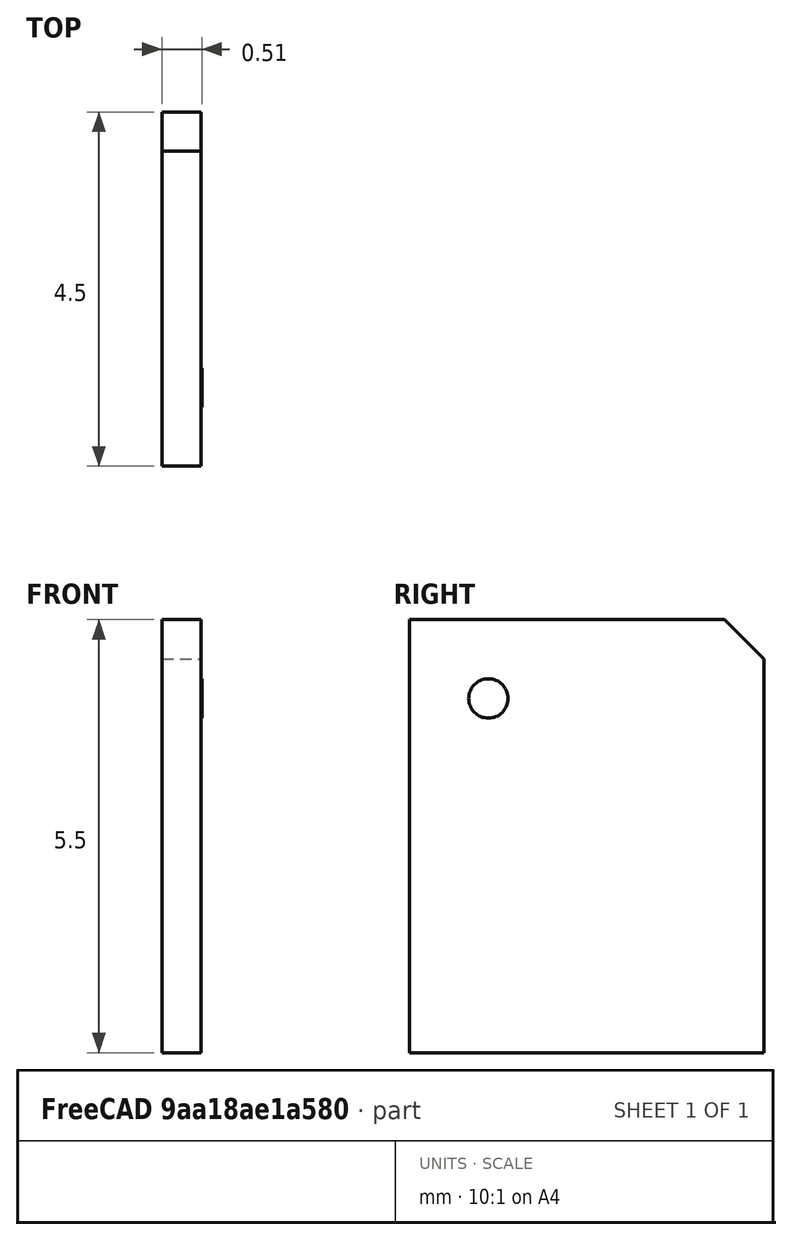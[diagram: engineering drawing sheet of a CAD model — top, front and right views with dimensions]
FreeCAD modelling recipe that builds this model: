
FCSTD DOCUMENT  (FreeCAD 1.1R20260108 (Git shallow))
Label: LiNbO3_Substrate_5mm
License: All rights reserved
LicenseURL: https://en.wikipedia.org/wiki/All_rights_reserved
objects: TechDraw::DrawViewAnnotation×5, TechDraw::DrawViewDimension×4, Sketcher::SketchObject×2, PartDesign::Pad×2, TechDraw::DrawProjGroupItem×2, App::Point×1, TechDraw::DrawSVGTemplate×1, PartDesign::Body×1, TechDraw::DrawProjGroup×1, TechDraw::DrawPage×1
note: 19 computed .brp shape members not serialized (recipe doc carries the construction recipe); baked Part::Feature solids carry a one-line shape summary decoded from their .brp

FEATURE [App::Point] Origin001
  Role = Origin
FEATURE [Sketcher::SketchObject] Sketch
  ArcFitTolerance = 1e-06
  AttachmentSupport = -> [Origin]
  ExternalTypes = [0]
  FullyConstrained = true
  MakeInternals = false
  MapMode = 5
  Placement = pos=(0,0,0) rot=(0.57735,0.57735,0.57735;2.0944rad)
  sketch-geometry (9):
    g0: LineSegment [constr] StartX=-2.25 StartY=-2.75 StartZ=0 EndX=2.25 EndY=-2.75 EndZ=0
    g1: LineSegment [constr] StartX=2.25 StartY=-2.75 StartZ=0 EndX=2.25 EndY=2.75 EndZ=0
    g2: LineSegment [constr] StartX=2.25 StartY=2.75 StartZ=0 EndX=-2.25 EndY=2.75 EndZ=0
    g3: LineSegment [constr] StartX=-2.25 StartY=2.75 StartZ=0 EndX=-2.25 EndY=-2.75 EndZ=0
    g4: LineSegment StartX=-2.25 StartY=-2.75 StartZ=0 EndX=2.25 EndY=-2.75 EndZ=0
    g5: LineSegment StartX=2.25 StartY=-2.75 StartZ=0 EndX=2.25 EndY=2.25 EndZ=0
    g6: LineSegment StartX=1.75 StartY=2.75 StartZ=0 EndX=2.25 EndY=2.25 EndZ=0
    g7: LineSegment StartX=1.75 StartY=2.75 StartZ=0 EndX=-2.25 EndY=2.75 EndZ=0
    g8: LineSegment StartX=-2.25 StartY=2.75 StartZ=0 EndX=-2.25 EndY=-2.75 EndZ=0
  constraints (24):
    c: Coincident(g0,g1)
    c: Coincident(g1,g2)
    c: Coincident(g2,g3)
    c: Coincident(g3,g0)
    c: Horizontal(g0)
    c: Horizontal(g2)
    c: Vertical(g1)
    c: Vertical(g3)
    c: Distance(g2,g2) = 4.5
    c: DistanceX(g-2,g2) = -2.25
    c: DistanceY(g-1,g0) = -2.75
    c: Coincident(g4,g0)
    c: Coincident(g4,g0)
    c: Coincident(g5,g0)
    c: PointOnObject(g5,g1)
    c: PointOnObject(g6,g2)
    c: Coincident(g6,g5)
    c: Distance(g5,g1) = 0.5
    c: Distance(g1,g6) = 0.5
    c: Coincident(g7,g6)
    c: Coincident(g7,g2)
    c: Coincident(g8,g2)
    c: Coincident(g8,g0)
    c: DistanceY(g8,g8) = 5.5
FEATURE [PartDesign::Pad] Pad
  Direction = (1,0,0)
  Length = 0.5
  Length2 = 10
  Profile = -> Sketch
  ReferenceAxis = -> Sketch [N_Axis]
  Refine = true
  SideType = 0
  Suppressed = false
  Type = 0
  Type2 = 0
FEATURE [TechDraw::DrawSVGTemplate] Template
  Height = 210
  Orientation = 1
  Template = /Applications/FreeCAD.app/Contents/Resources/share/Mod/TechDraw/Templates/ISO/A4_Landscape_TD.svg
  Width = 297
FEATURE [Sketcher::SketchObject] Sketch001
  ArcFitTolerance = 1e-06
  AttachmentSupport = -> [Pad]
  ExternalGeometry = -> [Pad]
  ExternalTypes = [0,0]
  FullyConstrained = true
  MakeInternals = false
  MapMode = 5
  Placement = pos=(0.5,0,0) rot=(0.57735,0.57735,0.57735;2.0944rad)
  sketch-geometry (1):
    g0: Circle CenterX=-1.25 CenterY=1.75 CenterZ=0 NormalX=0 NormalY=0 NormalZ=1 AngleXU=0 Radius=0.25
  constraints (3):
    c: DistanceY(g0,g-4) = 1
    c: DistanceX(g-4,g0) = 1
    c: Diameter(g0) = 0.5
FEATURE [PartDesign::Pad] Pad001
  BaseFeature = -> Pad
  Direction = (1,0,0)
  Length = 0.01
  Length2 = 10
  Profile = -> Sketch001
  ReferenceAxis = -> Sketch001 [N_Axis]
  Refine = true
  SideType = 0
  Suppressed = false
  Type = 0
  Type2 = 0
FEATURE [PartDesign::Body] Body
  AllowCompound = false
  Group = -> [Sketch,Pad,Sketch001,Pad001]
  Origin = -> Origin
  Tip = -> Pad001
FEATURE [TechDraw::DrawProjGroupItem] ProjItem  label="Front"
  CoarseView = false
  Direction = (1,0,0)
  Focus = 100
  HardHidden = true
  IsoCount = 0
  IsoHidden = false
  IsoVisible = false
  LockPosition = true
  Perspective = false
  Rotation = 0
  RotationVector = (0,1,0)
  Scale = 10
  ScaleType = 2
  ScrubCount = 1
  SeamHidden = false
  SeamVisible = false
  SmoothHidden = false
  SmoothVisible = true
  Source = -> [Body]
  Type = 0
  X = 0
  XDirection = (0,1,0)
  Y = 0
FEATURE [TechDraw::DrawProjGroupItem] ProjItem001  label="FrontTopRight"
  CoarseView = false
  Direction = (0.57735,0.57735,0.57735)
  Focus = 100
  HardHidden = true
  IsoCount = 0
  IsoHidden = false
  IsoVisible = false
  LockPosition = false
  Perspective = false
  Rotation = 0
  RotationVector = (1,0,0)
  Scale = 10
  ScaleType = 2
  ScrubCount = 1
  SeamHidden = false
  SeamVisible = false
  SmoothHidden = false
  SmoothVisible = true
  Source = -> [Body]
  Type = 7
  X = -55.1777
  XDirection = (-0.707107,0.707107,0)
  Y = -75.1599
FEATURE [TechDraw::DrawProjGroup] ProjGroup
  Anchor = -> ProjItem
  AutoDistribute = true
  LockPosition = false
  ProjectionType = 0
  Rotation = 0
  Scale = 10
  ScaleType = 2
  Source = -> [Body]
  Views = -> [ProjItem,ProjItem001]
  X = 151.849
  Y = 139.602
  spacingX = 15
  spacingY = 15
FEATURE [TechDraw::DrawViewAnnotation] Annotation
  Font = osifont
  LineSpace = 100
  LockPosition = false
  MaxWidth = -1
  Rotation = 0
  ScaleType = 0
  Text = +Z
  TextSize = 5
  TextStyle = 0
  X = 96.6709
  Y = 111.686
FEATURE [TechDraw::DrawViewAnnotation] Annotation001
  Font = osifont
  LineSpace = 100
  LockPosition = false
  MaxWidth = -1
  Rotation = 0
  ScaleType = 0
  Text = +Y
  TextSize = 5
  TextStyle = 0
  X = 130.594
  Y = 45.2038
FEATURE [TechDraw::DrawViewAnnotation] Annotation002
  Font = osifont
  LineSpace = 100
  LockPosition = false
  MaxWidth = -1
  Rotation = 0
  ScaleType = 0
  Text = +X
  TextSize = 5
  TextStyle = 0
  X = 62.0127
  Y = 47.1876
FEATURE [TechDraw::DrawViewDimension] Dimension
  AngleOverride = false
  Arbitrary = false
  ArbitraryTolerances = false
  BoxCorners = (2) [(-22.5,-27.5,0),(22.5,27.5,0)]
  EqualTolerance = true
  ExtensionAngle = 0
  FormatSpec = %.2w
  FormatSpecOverTolerance = %+.2w
  FormatSpecUnderTolerance = %+.2w
  Inverted = false
  LineAngle = 0
  LockPosition = false
  MeasureType = 1
  OverTolerance = 0.2
  References2D = -> [ProjItem]
  Rotation = 0
  ScaleType = 0
  ShowUnits = false
  TheoreticalExact = false
  Type = 1
  UnderTolerance = -0.2
  UseActualArea = true
  X = 0
  Y = -33.7508
FEATURE [TechDraw::DrawViewDimension] Dimension001
  AngleOverride = false
  Arbitrary = false
  ArbitraryTolerances = false
  BoxCorners = (2) [(-22.5,-27.5,0),(22.5,27.5,0)]
  EqualTolerance = true
  ExtensionAngle = 0
  FormatSpec = %.2w
  FormatSpecOverTolerance = %+.2w
  FormatSpecUnderTolerance = %+.2w
  Inverted = false
  LineAngle = 0
  LockPosition = false
  MeasureType = 1
  OverTolerance = 0.2
  References2D = -> [ProjItem]
  Rotation = 0
  ScaleType = 0
  ShowUnits = false
  TheoreticalExact = false
  Type = 2
  UnderTolerance = -0.2
  UseActualArea = true
  X = -37.7286
  Y = 0
FEATURE [TechDraw::DrawViewDimension] Dimension002
  AngleOverride = false
  Arbitrary = true
  ArbitraryTolerances = false
  BoxCorners = (2) [(-22.5,-27.5,0),(22.5,27.5,0)]
  EqualTolerance = true
  ExtensionAngle = 0
  FormatSpec = approx. 1.0
  FormatSpecOverTolerance = %+.2w
  FormatSpecUnderTolerance = %+.2w
  Inverted = false
  LineAngle = 0
  LockPosition = false
  MeasureType = 1
  OverTolerance = 0
  References2D = -> [ProjItem]
  Rotation = 0
  ScaleType = 0
  ShowUnits = false
  TheoreticalExact = false
  Type = 1
  UnderTolerance = 0
  UseActualArea = true
  X = -39.78
  Y = 39.0189
FEATURE [TechDraw::DrawViewDimension] Dimension003
  AngleOverride = false
  Arbitrary = true
  ArbitraryTolerances = false
  BoxCorners = (2) [(-22.5,-27.5,0),(22.5,27.5,0)]
  EqualTolerance = true
  ExtensionAngle = 0
  FormatSpec = approx. 0.5
  FormatSpecOverTolerance = %+.2w
  FormatSpecUnderTolerance = %+.2w
  Inverted = false
  LineAngle = 0
  LockPosition = false
  MeasureType = 1
  OverTolerance = 0
  References2D = -> [ProjItem]
  Rotation = 0
  ScaleType = 0
  ShowUnits = false
  TheoreticalExact = false
  Type = 1
  UnderTolerance = 0
  UseActualArea = true
  X = 41.2786
  Y = 39.0189
FEATURE [TechDraw::DrawViewAnnotation] Annotation003
  Font = osifont
  LineSpace = 100
  LockPosition = false
  MaxWidth = -1
  Rotation = 0
  ScaleType = 0
  Text = dye mark on +X face
  TextSize = 5
  TextStyle = 0
  X = 96.6709
  Y = 189.113
FEATURE [TechDraw::DrawViewAnnotation] Annotation004
  Font = osifont
  LineSpace = 100
  LockPosition = false
  MaxWidth = -1
  Rotation = 0
  ScaleType = 0
  Text = visible chamfer
  TextSize = 5
  TextStyle = 0
  X = 199.162
  Y = 189.113
FEATURE [TechDraw::DrawPage] Page
  KeepUpdated = true
  NextBalloonIndex = 1
  ProjectionType = 0
  Template = -> Template
  Views = -> [ProjGroup,Annotation,Annotation001,Annotation002,Dimension,Dimension001,Dimension002,Dimension003,Annotation003,Annotation004]
